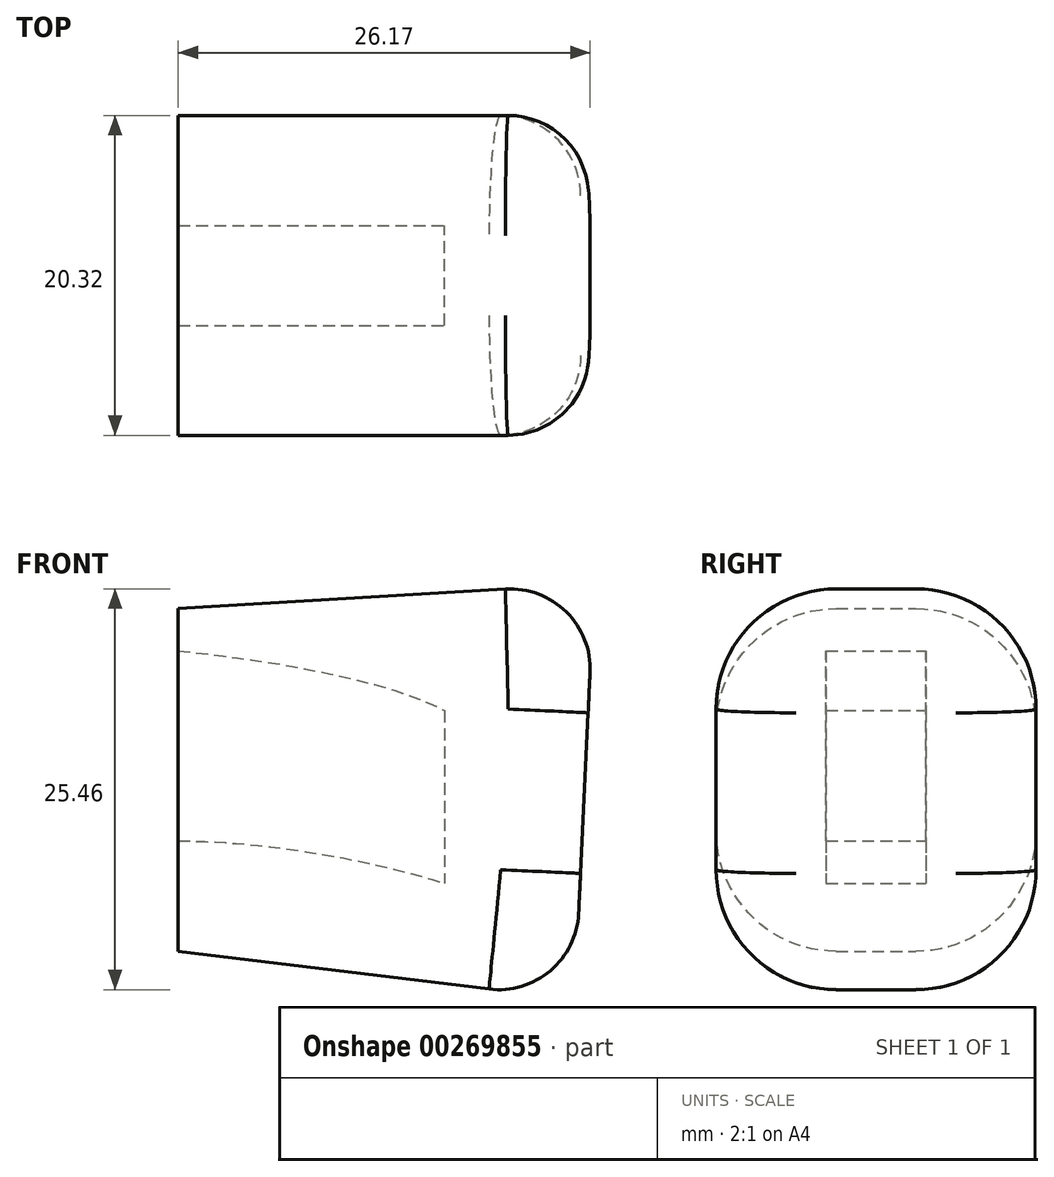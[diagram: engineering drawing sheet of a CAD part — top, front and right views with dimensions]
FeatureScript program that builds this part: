
annotation { "Feature Type Name" : "Feature", "Feature Type Description" : "" }
export const myFeature = defineFeature(function(context is Context, id is Id, definition is map)
    precondition{}
    {
        {
            var Q0;
            Q0=qCreatedBy(makeId("Front.planeOp"),FACE);
            var sketch = newSketch(context, id + "F0", { "sketchPlane" : qUnion([Q0])});
            skLineSegment(sketch, "E0", {"start": v(-23.5, -8.2) * mm, "end": v(-23.5, 13.57) * mm});
            skLineSegment(sketch, "E1", {"start": v(-23.5, 13.57) * mm, "end": v(2.93, 15.16) * mm});
            skLineSegment(sketch, "E2", {"start": v(2.93, 15.16) * mm, "end": v(1.68, -11.25) * mm});
            skLineSegment(sketch, "E3", {"start": v(1.68, -11.25) * mm, "end": v(-23.5, -8.2) * mm});
            skSolve(sketch);
        }
        {
            var Q0;
            Q0=makeQuery(id+"F0.imprint","IMPRINT",FACE,{"disambiguationData":[TD([[makeQuery(id+"F0.imprint","IMPRINT",EDGE,{"derivedFrom":sQuery(id+"F0.wireOp",EDGE,"E0")}),-1.0]])]});
            extrude(context, id + "F1", {"entities" : qUnion([Q0]), "depth" : 10.16 * mm, "hasSecondDirection" : true, "secondDirectionOppositeDirection" : true, "secondDirectionDepth" : 10.16 * mm});
        }
        {
            var Q0;
            Q0=qCreatedBy(makeId("Front.planeOp"),FACE);
            var sketch = newSketch(context, id + "F2", { "sketchPlane" : qUnion([Q0])});
            skLineSegment(sketch, "E4", {"start": v(-23.57, 10.9) * mm, "end": v(-23.57, -1.2) * mm});
            skLineSegment(sketch, "E5", {"start": v(-6.59, 7.1) * mm, "end": v(-6.59, -3.88) * mm});
            skFitSpline(sketch, "E6", {"points": [v(-23.57, 10.9) * mm, v(-6.59, 7.1) * mm], "startDerivative": vector(22.6, -2.3) * mm, "endDerivative": vector(10.07, -5.18) * mm});
            skFitSpline(sketch, "E7", {"points": [v(-23.57, -1.2) * mm, v(-6.59, -3.88) * mm], "startDerivative": vector(11.94, 0.14) * mm, "endDerivative": vector(17.84, -5.76) * mm});
            skSolve(sketch);
        }
        {
            var Q0;
            Q0 = qSketchRegion(id + "F2", true);
            extrude(context, id + "F3", {"entities" : qUnion([Q0]), "operationType" : NewBodyOperationType.REMOVE, "depth" : 3.17 * mm, "hasSecondDirection" : true, "secondDirectionOppositeDirection" : true, "secondDirectionDepth" : 3.17 * mm});
        }
        {
            var Q0;
            Q0=makeQuery(id+"F1.opExtrude","CAP_EDGE",EDGE,{"disambiguationData":[OSD([sQuery(id+"F0.wireOp",EDGE,"E1")])],"isStart":false});
            var Q1;
            Q1=makeQuery(id+"F1.opExtrude","CAP_EDGE",EDGE,{"disambiguationData":[OSD([sQuery(id+"F0.wireOp",EDGE,"E1")])],"isStart":true});
            var Q2;
            Q2=makeQuery(id+"F1.opExtrude","CAP_EDGE",EDGE,{"disambiguationData":[OSD([sQuery(id+"F0.wireOp",EDGE,"E3")])],"isStart":true});
            var Q3;
            Q3=makeQuery(id+"F1.opExtrude","CAP_EDGE",EDGE,{"disambiguationData":[OSD([sQuery(id+"F0.wireOp",EDGE,"E3")])],"isStart":false});
            fillet(context, id + "F4", {"entities" : qUnion([Q0, Q1, Q2, Q3]), "radius" : 7.62 * mm, "tangentPropagation" : true, "allowEdgeOverflow" : false});
        }
        {
            var Q0;
            Q0=makeQuery(id+"F1.opExtrude","SWEPT_FACE",FACE,{"disambiguationData":[OSD([sQuery(id+"F0.wireOp",EDGE,"E2")])]});
            fillet(context, id + "F5", {"entities" : qUnion([Q0]), "radius" : 5.08 * mm, "tangentPropagation" : true, "allowEdgeOverflow" : false});
        }
    });
